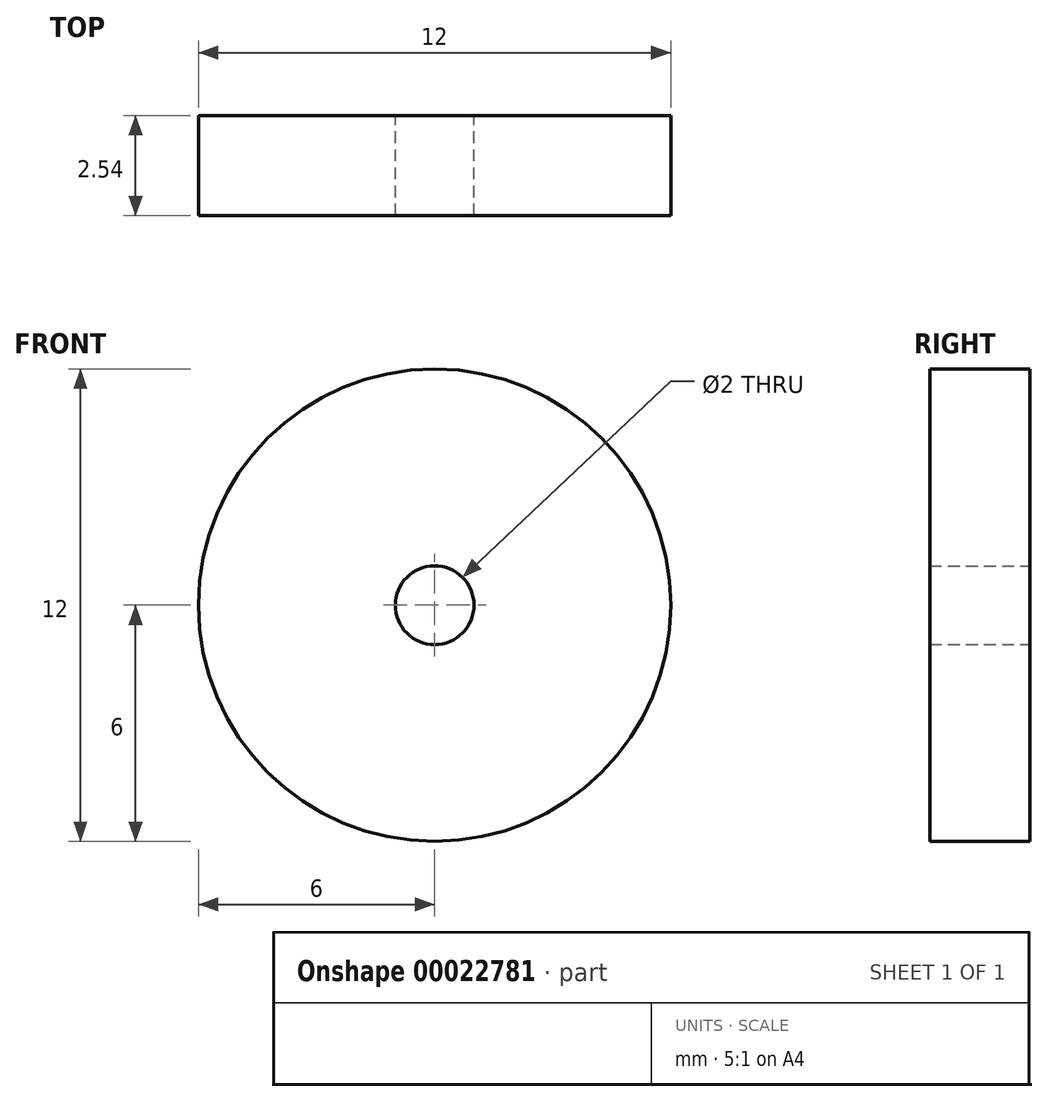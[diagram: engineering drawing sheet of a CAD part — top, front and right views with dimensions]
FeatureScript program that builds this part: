
annotation { "Feature Type Name" : "Feature", "Feature Type Description" : "" }
export const myFeature = defineFeature(function(context is Context, id is Id, definition is map)
    precondition{}
    {
        {
            var Q0;
            Q0=qCreatedBy(makeId("Front.planeOp"),FACE);
            var sketch = newSketch(context, id + "F0", { "sketchPlane" : qUnion([Q0])});
            skCircle(sketch, "E0", {"center": v(0, 0) * mm, "radius": 6 * mm});
            skCircle(sketch, "E1", {"center": v(0, 0) * mm, "radius": 1 * mm});
            skSolve(sketch);
        }
        {
            var Q0;
            Q0=makeQuery(id+"F0.imprint","IMPRINT",FACE,{"disambiguationData":[TD([[makeQuery(id+"F0.imprint","IMPRINT",EDGE,{"derivedFrom":sQuery(id+"F0.wireOp",EDGE,"E0")}),1.0]])]});
            extrude(context, id + "F1", {"entities" : qUnion([Q0]), "depth" : 2.54 * mm});
        }
    });
